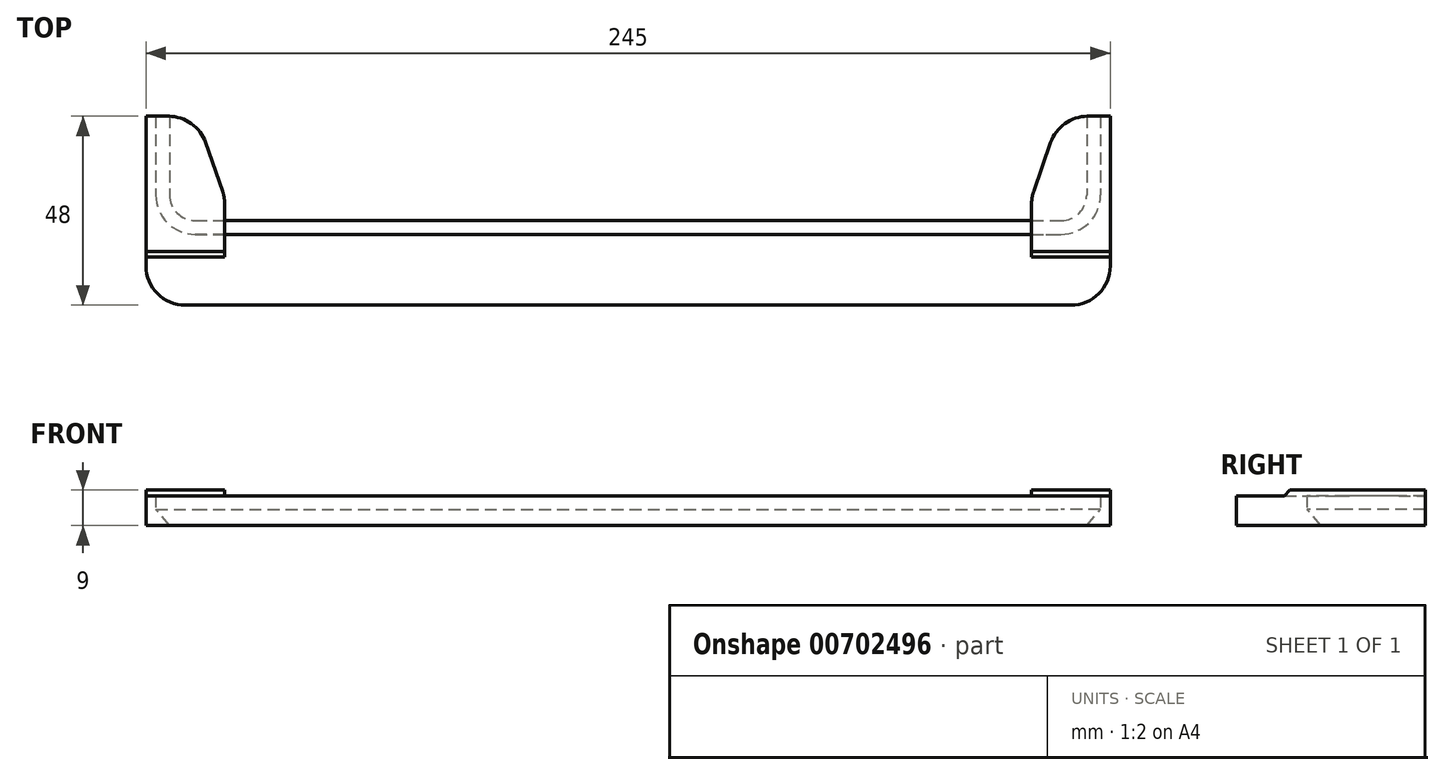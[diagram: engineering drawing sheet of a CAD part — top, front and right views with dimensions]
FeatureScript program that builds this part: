
annotation { "Feature Type Name" : "Feature", "Feature Type Description" : "" }
export const myFeature = defineFeature(function(context is Context, id is Id, definition is map)
    precondition{}
    {
        {
            var Q0;
            Q0=qCreatedBy(makeId("Top.planeOp"),FACE);
            var sketch = newSketch(context, id + "F0", { "sketchPlane" : qUnion([Q0])});
            skLineSegment(sketch, "E0.bottom", {"start": v(122.5, -9) * mm, "end": v(-122.5, -9) * mm});
            skLineSegment(sketch, "E0.top", {"start": v(122.5, 9) * mm, "end": v(-122.5, 9) * mm});
            skLineSegment(sketch, "E0.left", {"start": v(122.5, -9) * mm, "end": v(122.5, 9) * mm});
            skLineSegment(sketch, "E0.right", {"start": v(-122.5, -9) * mm, "end": v(-122.5, 9) * mm});
            skPoint(sketch, "E0.middle", {"position": v(0, 0) * mm});
            skLineSegment(sketch, "E1", {"start": v(0, 9) * mm, "end": v(0, -9) * mm});
            skSolve(sketch);
        }
        {
            var Q0;
            {var subQ0=sQuery(id+"F0.wireOp",EDGE,"E0.right");Q0=makeQuery(id+"F0.imprint","IMPRINT",FACE,{"disambiguationData":[TD([[makeQuery(id+"F0.imprint","IMPRINT",EDGE,{"derivedFrom":subQ0}),-1.0]])]});}
            extrude(context, id + "F1", {"entities" : qUnion([Q0]), "depth" : 7.6 * mm, "offsetDistance" : 25 * mm});
        }
        {
            var Q0;
            Q0=qCreatedBy(makeId("Top.planeOp"),FACE);
            var sketch = newSketch(context, id + "F2", { "sketchPlane" : qUnion([Q0])});
            skLineSegment(sketch, "E2.bottom", {"start": v(122.5, 39) * mm, "end": v(-122.5, 39) * mm});
            skLineSegment(sketch, "E2.top", {"start": v(122.5, 9) * mm, "end": v(-122.5, 9) * mm});
            skLineSegment(sketch, "E2.left", {"start": v(122.5, 39) * mm, "end": v(122.5, 9) * mm});
            skLineSegment(sketch, "E2.right", {"start": v(-122.5, 39) * mm, "end": v(-122.5, 9) * mm});
            skPoint(sketch, "E2.middle", {"position": v(0, 0) * mm});
            skLineSegment(sketch, "E3", {"start": v(-120, 39) * mm, "end": v(-120, 19) * mm});
            skLineSegment(sketch, "E4", {"start": v(-110, 9) * mm, "end": v(0, 9) * mm});
            skPoint(sketch, "E4.endSnap0", {"position": v(0, 9) * mm});
            skLineSegment(sketch, "E5", {"start": v(0, 9) * mm, "end": v(0, 9) * mm});
            skArc(sketch, "E6.filletArc", {"start": v(-120, 19) * mm, "mid": v(-117.07, 11.93) * mm, "end": v(-110, 9) * mm});
            skSolve(sketch);
        }
        {
            var Q0;
            {var subQ0=sQuery(id+"F2.wireOp",EDGE,"E2.right");Q0=makeQuery(id+"F2.imprint","IMPRINT",FACE,{"disambiguationData":[TD([[makeQuery(id+"F2.imprint","IMPRINT",EDGE,{"derivedFrom":subQ0}),1.0]])]});}
            extrude(context, id + "F3", {"entities" : qUnion([Q0]), "operationType" : NewBodyOperationType.ADD, "depth" : 7.6 * mm, "offsetDistance" : 25 * mm});
        }
        {
            var Q0;
            Q0=qCreatedBy(makeId("Top.planeOp"),FACE);
            var sketch = newSketch(context, id + "F4", { "sketchPlane" : qUnion([Q0])});
            skLineSegment(sketch, "E7.right", {"start": v(-122.5, 39) * mm, "end": v(-122.5, 9) * mm});
            skPoint(sketch, "E7.middle", {"position": v(0, 0) * mm});
            skLineSegment(sketch, "E8", {"start": v(-120, 39) * mm, "end": v(-120, 19) * mm});
            skLineSegment(sketch, "E9", {"start": v(-110, 9) * mm, "end": v(0, 9) * mm});
            skArc(sketch, "E10.filletArc", {"start": v(-120, 19) * mm, "mid": v(-117.07, 11.93) * mm, "end": v(-110, 9) * mm});
            skLineSegment(sketch, "E11.0", {"start": v(-110, 12.5) * mm, "end": v(0.27, 12.5) * mm});
            skArc(sketch, "E11.1", {"start": v(-116.5, 19) * mm, "mid": v(-114.6, 14.4) * mm, "end": v(-110, 12.5) * mm});
            skLineSegment(sketch, "E11.2", {"start": v(-116.5, 39) * mm, "end": v(-116.5, 19) * mm});
            skLineSegment(sketch, "E12", {"start": v(-116.5, 39) * mm, "end": v(-120, 39) * mm});
            skLineSegment(sketch, "E13", {"start": v(0.27, 12.5) * mm, "end": v(0, 9) * mm});
            skSolve(sketch);
        }
        {
            var Q0;
            Q0 = qSketchRegion(id + "F4", true);
            extrude(context, id + "F5", {"entities" : qUnion([Q0]), "operationType" : NewBodyOperationType.ADD, "depth" : 5 * mm, "offsetDistance" : 25 * mm});
        }
        {
            var Q0;
            Q0=makeQuery(id+"F5.opExtrude","CAP_EDGE",EDGE,{"disambiguationData":[OSD([sQuery(id+"F4.wireOp",EDGE,"E11.2")])],"isStart":false});
            var Q1;
            Q1=makeQuery(id+"F5.opExtrude","CAP_EDGE",EDGE,{"disambiguationData":[OSD([sQuery(id+"F4.wireOp",EDGE,"E11.1")])],"isStart":false});
            chamfer(context, id + "F6", {"entities" : qUnion([Q0, Q1]), "chamferType" : ChamferType.OFFSET_ANGLE, "width" : 5 * mm, "oppositeDirection" : false, "angle" : 40 * degree, "tangentPropagation" : true});
        }
        {
            var Q0;
            Q0=qCreatedBy(makeId("Top.planeOp"),FACE);
            var sketch = newSketch(context, id + "F7", { "sketchPlane" : qUnion([Q0])});
            skLineSegment(sketch, "E14.bottom", {"start": v(-122.5, 1.65) * mm, "end": v(-102.5, 1.65) * mm});
            skLineSegment(sketch, "E14.left", {"start": v(-122.5, 1.65) * mm, "end": v(-122.5, 39) * mm});
            skLineSegment(sketch, "E14.right", {"start": v(-102.5, 1.65) * mm, "end": v(-102.5, 16.74) * mm});
            skLineSegment(sketch, "E15", {"start": v(-122.5, 39) * mm, "end": v(-116.77, 39) * mm});
            skLineSegment(sketch, "E16", {"start": v(-107.32, 32.29) * mm, "end": v(-103.06, 20.03) * mm});
            skPoint(sketch, "E17.visualSharp", {"position": v(-102.5, 18.43) * mm});
            skArc(sketch, "E17.filletArc", {"start": v(-102.5, 16.74) * mm, "mid": v(-102.64, 18.4) * mm, "end": v(-103.06, 20.03) * mm});
            skPoint(sketch, "E18.visualSharp", {"position": v(-109.66, 39) * mm});
            skArc(sketch, "E18.filletArc", {"start": v(-107.32, 32.29) * mm, "mid": v(-110.97, 37.15) * mm, "end": v(-116.77, 39) * mm});
            skSolve(sketch);
        }
        {
            var Q0;
            Q0 = qSketchRegion(id + "F7", true);
            var Q1;
            Q1=makeQuery(id+"F3.boolean.opBoolean","MERGE",FACE,{"derivedFrom":[makeQuery(id+"F1.opExtrude","CAP_FACE",FACE,{"disambiguationData":[OSD([sQuery(id+"F0.wireOp",EDGE,"E0.bottom"),sQuery(id+"F0.wireOp",EDGE,"E0.top"),sQuery(id+"F0.wireOp",EDGE,"E0.left"),sQuery(id+"F0.wireOp",EDGE,"E0.right")])],"isStart":false}),makeQuery(id+"F3.opExtrude","CAP_FACE",FACE,{"disambiguationData":[OSD([sQuery(id+"F2.wireOp",EDGE,"E2.bottom"),sQuery(id+"F2.wireOp",EDGE,"E2.top"),sQuery(id+"F2.wireOp",EDGE,"E2.right"),sQuery(id+"F2.wireOp",EDGE,"E3"),sQuery(id+"F2.wireOp",EDGE,"E4"),sQuery(id+"F2.wireOp",EDGE,"E5"),sQuery(id+"F2.wireOp",EDGE,"E6.filletArc")])],"isStart":false})]});
            extrude(context, id + "F8", {"entities" : qUnion([Q0]), "operationType" : NewBodyOperationType.ADD, "depth" : 9 * mm, "offsetDistance" : 25 * mm, "hasSecondDirection" : true, "secondDirectionBound" : SecondDirectionBoundingType.UP_TO_SURFACE, "secondDirectionOppositeDirection" : false, "secondDirectionDepth" : 5 * mm, "secondDirectionBoundEntityFace" : qUnion([Q1])});
        }
        {
            var Q0;
            Q0=makeQuery(id+"F8.opExtrude","CAP_EDGE",EDGE,{"disambiguationData":[OSD([sQuery(id+"F7.wireOp",EDGE,"E14.bottom")])],"isStart":false});
            chamfer(context, id + "F9", {"entities" : qUnion([Q0]), "width" : 3 * mm, "tangentPropagation" : true});
        }
        {
            var Q0;
            Q0=makeQuery(id+"F1.opExtrude","SWEPT_EDGE",EDGE,{"disambiguationData":[OSD([sQuery(id+"F0.wireOp",EDGE,"E0.bottom"),sQuery(id+"F0.wireOp",EDGE,"E0.right")])]});
            fillet(context, id + "F10", {"entities" : qUnion([Q0]), "radius" : 10 * mm, "tangentPropagation" : true, "allowEdgeOverflow" : false});
        }
        {
            var Q0;
            Q0=makeQuery(id+"F1.opExtrude","SWEPT_BODY",BODY,{"disambiguationData":[OSD([sQuery(id+"F0.wireOp",EDGE,"E0.bottom"),sQuery(id+"F0.wireOp",EDGE,"E0.top"),sQuery(id+"F0.wireOp",EDGE,"E0.right"),sQuery(id+"F0.wireOp",EDGE,"E1")])]});
            var Q1;
            Q1=qCreatedBy(makeId("Right.planeOp"),FACE);
            mirror(context, id + "F11", {"operationType" : NewBodyOperationType.ADD, "entities" : qUnion([Q0]), "mirrorPlane" : qUnion([Q1])});
        }
    });
